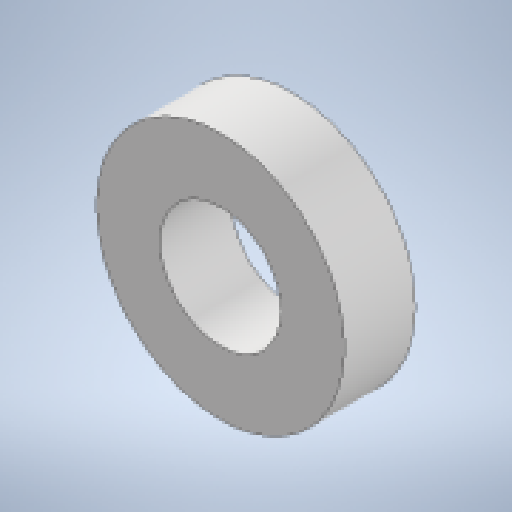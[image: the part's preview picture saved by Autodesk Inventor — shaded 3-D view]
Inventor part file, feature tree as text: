
AUTODESK INVENTOR PART (.ipt)
format: ipt  version: 2023 (Build 270158000, 158)  size: 135,168 bytes
history: native  units: in
note: dims shown in document units (in); Inventor stores cm internally (conversion verified against a paired STEP export)
features: extrude x1, sketch x1
ambient origin geometry x8: Origin, YZ Plane, XZ Plane, XY Plane, X Axis, Y Axis, Z Axis, Center Point
bodies: Solid1 (feature_tree)
feature tree (2):
  extrude  "Extrusion1"  Depth=0.28in
  sketch  "Sketch1"  dims[d0=1.378in d1=1.85in d2=0.28in d3=0.0in]
